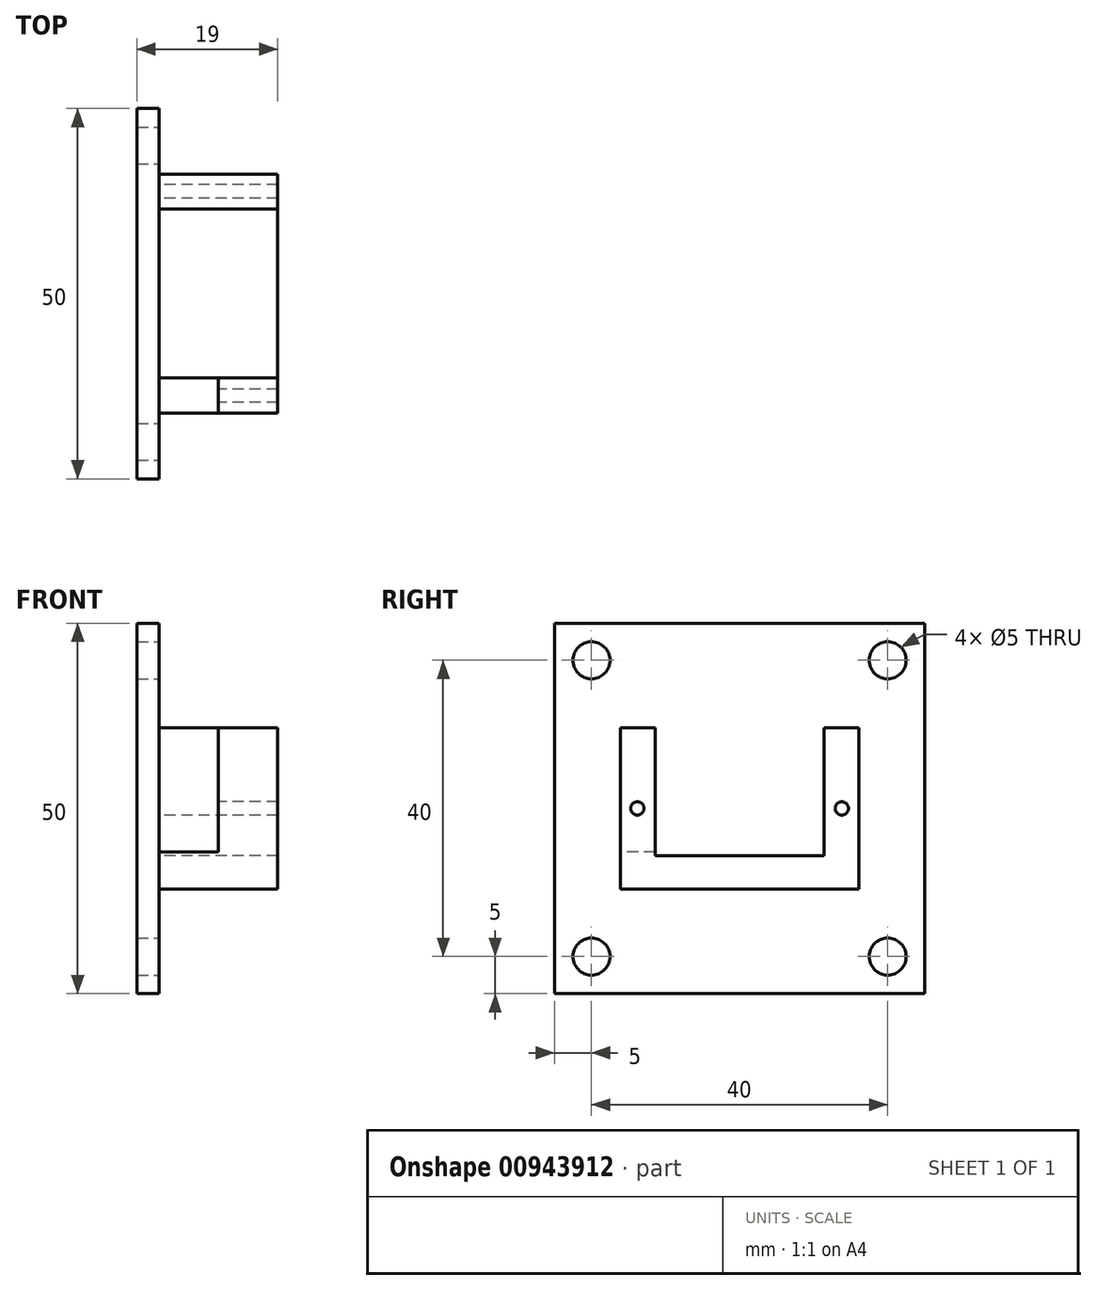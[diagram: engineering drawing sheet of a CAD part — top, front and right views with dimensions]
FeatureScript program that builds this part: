
annotation { "Feature Type Name" : "Feature", "Feature Type Description" : "" }
export const myFeature = defineFeature(function(context is Context, id is Id, definition is map)
    precondition{}
    {
        {
            var Q0;
            Q0=qCreatedBy(makeId("Right.planeOp"),FACE);
            var sketch = newSketch(context, id + "F0", { "sketchPlane" : qUnion([Q0])});
            skLineSegment(sketch, "E0.right", {"start": v(-16.1, 5.9) * mm, "end": v(-16.1, -5.9) * mm});
            skPoint(sketch, "E0.middle", {"position": v(0, 0) * mm});
            skLineSegment(sketch, "E1.right", {"start": v(11.4, 5.9) * mm, "end": v(11.4, -5.9) * mm});
            skLineSegment(sketch, "E2.right", {"start": v(3.3, 5.9) * mm, "end": v(3.3, -5.9) * mm, "construction": true});
            skCircle(sketch, "E3", {"center": v(-5.5, 0) * mm, "radius": 2.3 * mm, "construction": true});
            skLineSegment(sketch, "E4", {"start": v(-16.1, 0) * mm, "end": v(-13.8, 0) * mm, "construction": true});
            skLineSegment(sketch, "E5", {"start": v(16.1, 0) * mm, "end": v(13.8, 0) * mm, "construction": true});
            skCircle(sketch, "E6", {"center": v(-13.8, 0) * mm, "radius": 0.9 * mm});
            skCircle(sketch, "E7", {"center": v(13.8, 0) * mm, "radius": 0.9 * mm});
            skLineSegment(sketch, "E8", {"start": v(16.1, -5.9) * mm, "end": v(16.1, 5.9) * mm});
            skPoint(sketch, "E9.orphan", {"position": v(-16.1, 5.9) * mm});
            skLineSegment(sketch, "E10", {"start": v(3.3, 5.9) * mm, "end": v(11.4, 5.9) * mm, "construction": true});
            skPoint(sketch, "E11.0.midPoint", {"position": v(-11.8, 0) * mm});
            skPoint(sketch, "E12.0.midPoint", {"position": v(15.8, 0) * mm});
            skLineSegment(sketch, "E13.bottom", {"start": v(-11.4, 5.9) * mm, "end": v(11.4, 5.9) * mm, "construction": true});
            skLineSegment(sketch, "E13.top", {"start": v(-16.1, 10.9) * mm, "end": v(-11.4, 10.9) * mm});
            skLineSegment(sketch, "E13.left", {"start": v(-16.1, 5.9) * mm, "end": v(-16.1, 10.9) * mm});
            skLineSegment(sketch, "E13.right", {"start": v(16.1, 5.9) * mm, "end": v(16.1, 10.9) * mm});
            skLineSegment(sketch, "E14.top", {"start": v(16.1, -10.9) * mm, "end": v(-16.1, -10.9) * mm});
            skLineSegment(sketch, "E14.left", {"start": v(16.1, -5.9) * mm, "end": v(16.1, -10.9) * mm});
            skLineSegment(sketch, "E14.right", {"start": v(-16.1, -5.9) * mm, "end": v(-16.1, -10.9) * mm});
            skLineSegment(sketch, "E15", {"start": v(-11.4, 5.9) * mm, "end": v(-11.4, 10.9) * mm});
            skLineSegment(sketch, "E16", {"start": v(11.4, 5.9) * mm, "end": v(11.4, 10.9) * mm});
            skLineSegment(sketch, "E17", {"start": v(-11.4, 5.9) * mm, "end": v(-11.4, -5.9) * mm});
            skLineSegment(sketch, "E18.trimOffspring", {"start": v(11.4, 10.9) * mm, "end": v(16.1, 10.9) * mm});
            skLineSegment(sketch, "E19.bottom", {"start": v(-11.4, -5.9) * mm, "end": v(11.4, -5.9) * mm, "construction": true});
            skLineSegment(sketch, "E19.top", {"start": v(-11.4, -6.4) * mm, "end": v(11.4, -6.4) * mm});
            skLineSegment(sketch, "E19.left", {"start": v(-11.4, -5.9) * mm, "end": v(-11.4, -6.4) * mm});
            skLineSegment(sketch, "E19.right", {"start": v(11.4, -5.9) * mm, "end": v(11.4, -6.4) * mm});
            skSolve(sketch);
        }
        {
            var Q0;
            Q0 = qSketchRegion(id + "F0", true);
            extrude(context, id + "F1", {"entities" : qUnion([Q0]), "depth" : 16 * mm, "offsetDistance" : 25 * mm});
        }
        {
            var Q0;
            Q0=makeQuery(id+"F1.opExtrude","SWEPT_FACE",FACE,{"disambiguationData":[OSD([sQuery(id+"F0.wireOp",EDGE,"E0.right"),sQuery(id+"F0.wireOp",EDGE,"E13.left"),sQuery(id+"F0.wireOp",EDGE,"E14.right")])]});
            var sketch = newSketch(context, id + "F2", { "sketchPlane" : qUnion([Q0])});
            skLineSegment(sketch, "E20.bottom", {"start": v(0, 10.9) * mm, "end": v(8, 10.9) * mm});
            skLineSegment(sketch, "E20.top", {"start": v(0, -5.9) * mm, "end": v(8, -5.9) * mm});
            skLineSegment(sketch, "E20.left", {"start": v(0, 10.9) * mm, "end": v(0, -5.9) * mm});
            skLineSegment(sketch, "E20.right", {"start": v(8, 10.9) * mm, "end": v(8, -5.9) * mm});
            skSolve(sketch);
        }
        {
            var Q0;
            Q0 = qSketchRegion(id + "F2", true);
            extrude(context, id + "F3", {"entities" : qUnion([Q0]), "operationType" : NewBodyOperationType.REMOVE, "depth" : -5 * mm, "offsetDistance" : 25 * mm});
        }
        {
            var Q0;
            Q0=makeQuery(id+"F0.imprint","IMPRINT",FACE,{"disambiguationData":[TD([[makeQuery(id+"F0.imprint","IMPRINT",EDGE,{"derivedFrom":sQuery(id+"F0.wireOp",EDGE,"E0.right")}),1.0]])]});
            var sketch = newSketch(context, id + "F4", { "sketchPlane" : qUnion([Q0])});
            skLineSegment(sketch, "E21.bottom", {"start": v(-25, -25) * mm, "end": v(25, -25) * mm});
            skLineSegment(sketch, "E21.top", {"start": v(-25, 25) * mm, "end": v(25, 25) * mm});
            skLineSegment(sketch, "E21.left", {"start": v(-25, -25) * mm, "end": v(-25, 25) * mm});
            skLineSegment(sketch, "E21.right", {"start": v(25, -25) * mm, "end": v(25, 25) * mm});
            skPoint(sketch, "E21.middle", {"position": v(0, 0) * mm});
            skCircle(sketch, "E22", {"center": v(20, -20) * mm, "radius": 2.5 * mm});
            skCircle(sketch, "E23", {"center": v(-20, -20) * mm, "radius": 2.5 * mm});
            skCircle(sketch, "E24", {"center": v(-20, 20) * mm, "radius": 2.5 * mm});
            skCircle(sketch, "E25", {"center": v(20, 20) * mm, "radius": 2.5 * mm});
            skSolve(sketch);
        }
        {
            var Q0;
            Q0 = qSketchRegion(id + "F4", true);
            extrude(context, id + "F5", {"entities" : qUnion([Q0]), "operationType" : NewBodyOperationType.ADD, "depth" : -3 * mm, "offsetDistance" : 25 * mm});
        }
    });
